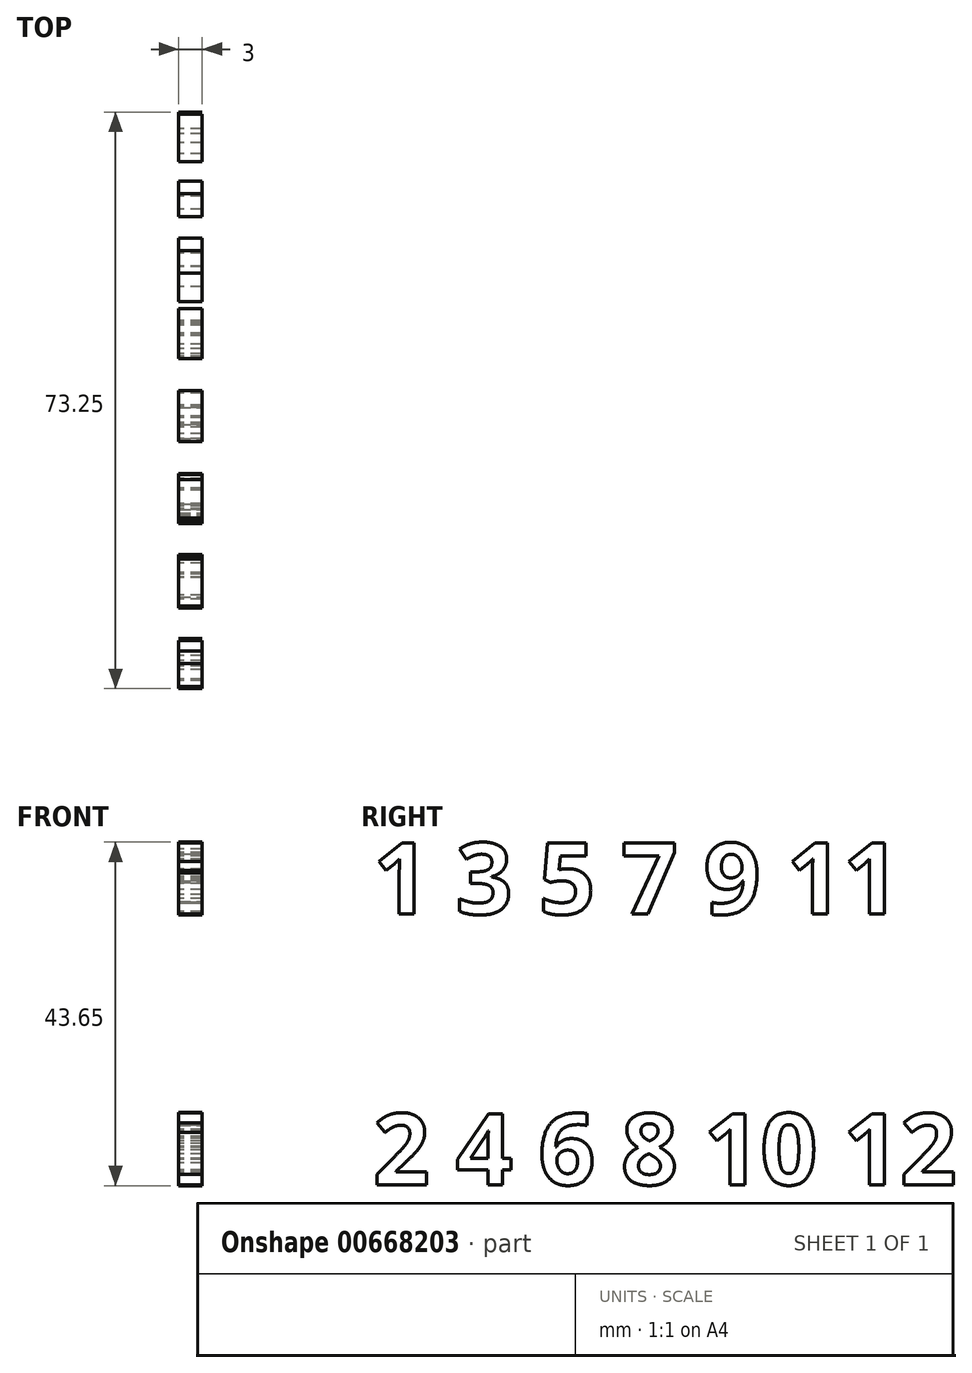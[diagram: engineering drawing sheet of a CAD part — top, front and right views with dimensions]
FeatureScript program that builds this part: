
annotation { "Feature Type Name" : "Feature", "Feature Type Description" : "" }
export const myFeature = defineFeature(function(context is Context, id is Id, definition is map)
    precondition{}
    {
        {
            var Q0;
            Q0=qCreatedBy(makeId("Right.planeOp"),FACE);
            var sketch = newSketch(context, id + "F0", { "sketchPlane" : qUnion([Q0])});
            skText(sketch, "E0", { "text": "1 3 5 7 9 11\n\n2 4 6 8 10 12", "fontName": "OpenSans-Bold.ttf"});
            const initialGuessF0  = {"E0": [-0.07459, 0, 1, 0, 0.0091]};
            skSetInitialGuess(sketch, initialGuessF0);
            skSolve(sketch);
        }
        {
            var Q0;
            Q0 = qSketchRegion(id + "F0", true);
            extrude(context, id + "F1", {"entities" : qUnion([Q0]), "depth" : 3 * mm, "offsetDistance" : 25 * mm});
        }
    });
